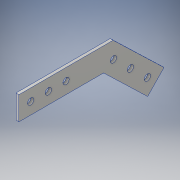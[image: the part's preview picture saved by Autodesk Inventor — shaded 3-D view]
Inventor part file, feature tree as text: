
AUTODESK INVENTOR PART (.ipt)
format: ipt  version: 2016 (Build 200138000, 138)  size: 129,024 bytes
history: native  units: in
note: dims shown in document units (in); Inventor stores cm internally (conversion verified against a paired STEP export)
features: extrude x2, sketch x2
ambient origin geometry x8: Origin, YZ Plane, XZ Plane, XY Plane, X Axis, Y Axis, Z Axis, Center Point
bodies: Solid1 (feature_tree)
feature tree (4):
  extrude  "Extrusion1"  Depth=1.0in
  extrude  "Extrusion2"  Depth=0.125in
  sketch  "Sketch1"  dims[d0=4.0in d1=1.0in]
  sketch  "Sketch2"  dims[d2=1.0in d3=3.0in d4=0.9351in d5=0.125in d6=0.0in d7=0.2656in d8=0.2656in d9=0.2656in d10=0.5in d11=0.75in d12=0.75in d13=0.125in d14=0.0in d15=0.2656in d16=0.2656in d17=0.2656in d18=0.5in d19=0.5in d20=0.5in d21=0.5in d22=1.5in d23=2.5in]
